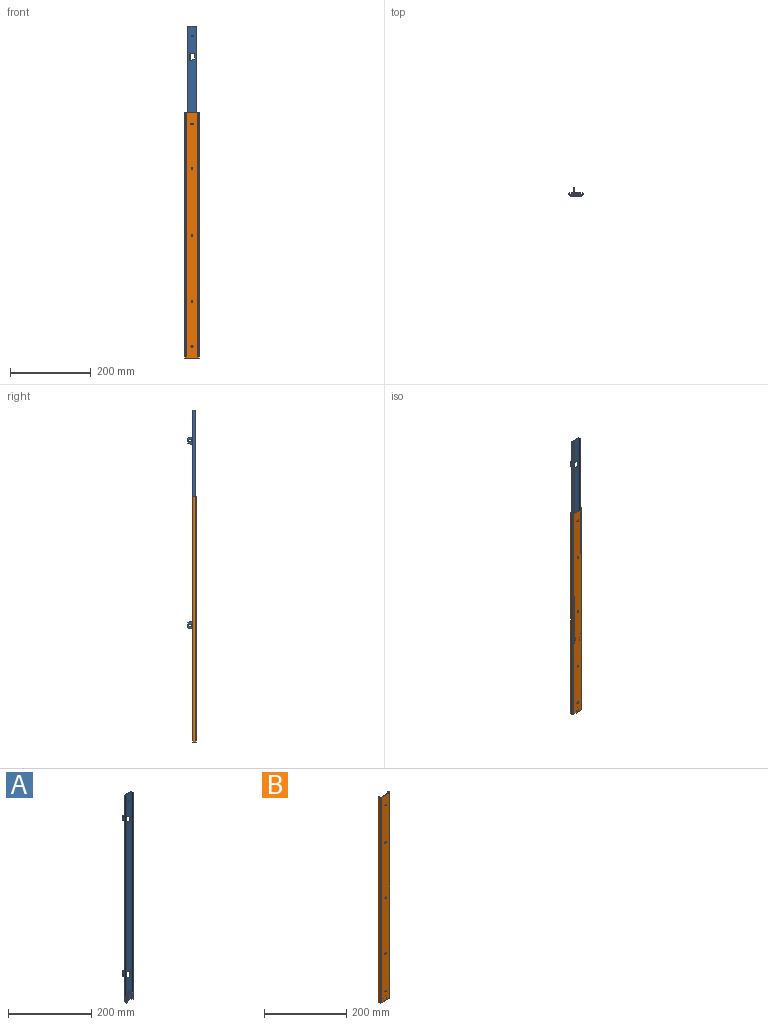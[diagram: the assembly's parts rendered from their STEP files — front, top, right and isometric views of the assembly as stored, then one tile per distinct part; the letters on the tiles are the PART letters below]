
ASSEMBLY  parts=2 mates=1
PART A: 102 faces, bbox 24.4x18.9x610 mm
  f0: plane 3.3x0.94mm, normal (0.82,0,0.57), area 3.8mm2, adj f8,f10,f28,f32
  f1: cylinder r=1mm len=3.3mm, axis (0,1,0), area 4.2mm2, adj f11,f12,f28,f32
  f2: cylinder r=1mm len=3.3mm, axis (0,1,0), area 3.2mm2, adj f7,f12,f28,f32
  f3: cylinder r=1mm len=3.3mm, axis (0,1,0), area 3.2mm2, adj f6,f13,f30,f32
  f4: cylinder r=1mm len=3.3mm, axis (0,1,0), area 4.2mm2, adj f13,f14,f30,f32
  f5: plane 3.3x0.94mm, normal (-0.82,0,0.57), area 3.8mm2, adj f9,f15,f30,f32
  f6: plane 3.3x0.17mm, normal (0.95,0,-0.3), area 0.6mm2, adj f3,f24,f30,f32
  f7: plane 3.3x0.17mm, normal (-0.95,0,-0.3), area 0.6mm2, adj f2,f26,f28,f32
  f8: cylinder r=1mm len=3.3mm, axis (0,1,0), area 4.2mm2, adj f0,f27,f28,f32
  f9: cylinder r=1mm len=3.3mm, axis (0,1,0), area 4.2mm2, adj f5,f29,f30,f32
  f10: cylinder r=1mm len=3.3mm, axis (0,1,0), area 10.4mm2, adj f0,f11,f28,f32
  f11: plane 3.3x2.58mm, normal (-0.82,0,-0.57), area 10.4mm2, adj f1,f10,f28,f32
  f12: plane 3.3x1.72mm, normal (-0.79,0,0.61), area 7.2mm2, adj f1,f2,f28,f32
  f13: plane 3.3x1.72mm, normal (0.79,0,0.61), area 7.2mm2, adj f3,f4,f30,f32
  f14: plane 3.3x2.58mm, normal (0.82,0,-0.57), area 10.4mm2, adj f4,f15,f30,f32
  f15: cylinder r=1mm len=3.3mm, axis (0,1,0), area 10.4mm2, adj f5,f14,f30,f32
  f16: cylinder r=1mm len=3.3mm, axis (0,1,0), area 4.2mm2, adj f19,f32,f34,f64
  f17: cylinder r=1mm len=3.3mm, axis (0,1,0), area 3.2mm2, adj f32,f33,f35,f64
  f18: cylinder r=1mm len=3.3mm, axis (0,1,0), area 4.2mm2, adj f32,f35,f36,f64
  f19: plane 3.3x0.94mm, normal (-0.82,0,-0.57), area 3.8mm2, adj f16,f32,f37,f64
  f20: cylinder r=1mm len=3.3mm, axis (0,1,0), area 4.2mm2, adj f21,f32,f38,f65
  f21: plane 3.3x0.94mm, normal (0.82,0,-0.57), area 3.8mm2, adj f20,f32,f39,f65
  f22: cylinder r=1mm len=3.3mm, axis (0,1,0), area 3.2mm2, adj f31,f32,f41,f65
  f23: cylinder r=1mm len=3.3mm, axis (0,1,0), area 4.2mm2, adj f32,f40,f41,f65
  f24: plane 4.8x2.5mm, normal (1,0,0), area 9.4mm2, adj f6,f25,f30,f32,f56
  f25: plane 13.8x1.5mm, normal (0,-0.71,0.71), area 29.3mm2, adj f24,f26,f32,f56
  f26: plane 4.8x2.5mm, normal (-1,0,0), area 9.4mm2, adj f7,f25,f28,f32,f56
  f27: plane 3.3x3.3mm, normal (0.79,0,-0.61), area 13.8mm2, adj f8,f28,f32,f58
  f28: plane 9.5x5.56mm, normal (0,-1,0), area 28.9mm2, adj f0,f1,f2,f7,f8,f10,f11,f12
  f29: plane 3.3x3.3mm, normal (-0.79,0,-0.61), area 13.8mm2, adj f9,f30,f32,f59
  f30: plane 9.5x5.56mm, normal (0,-1,0), area 28.9mm2, adj f3,f4,f5,f6,f9,f13,f14,f15
  f31: plane 3.3x0.17mm, normal (-0.95,0,0.3), area 0.6mm2, adj f22,f32,f61,f65
  f32: plane 21.6x16.5mm, normal (0,-1,0), area 268.1mm2, adj f0,f1,f2,f3,f4,f5,f6,f7
  f33: plane 3.3x0.17mm, normal (0.95,0,0.3), area 0.6mm2, adj f17,f32,f63,f64
  f34: plane 3.3x3.3mm, normal (-0.79,0,0.61), area 13.8mm2, adj f16,f32,f59,f64
  f35: plane 3.3x1.72mm, normal (0.79,0,-0.61), area 7.2mm2, adj f17,f18,f32,f64
  f36: plane 3.3x2.58mm, normal (0.82,0,0.57), area 10.4mm2, adj f18,f32,f37,f64
  f37: cylinder r=1mm len=3.3mm, axis (0,1,0), area 10.4mm2, adj f19,f32,f36,f64
  f38: plane 3.3x3.3mm, normal (0.79,0,0.61), area 13.8mm2, adj f20,f32,f58,f65
  f39: cylinder r=1mm len=3.3mm, axis (0,1,0), area 10.4mm2, adj f21,f32,f40,f65
  f40: plane 3.3x2.58mm, normal (-0.82,0,0.57), area 10.4mm2, adj f23,f32,f39,f65
  f41: plane 3.3x1.72mm, normal (-0.79,0,-0.61), area 7.2mm2, adj f22,f23,f32,f65
  f42: cylinder r=2mm len=1.99mm, axis (-1,0,0), area 4.1mm2, adj f44,f70,f71,f85
  f43: cylinder r=2mm len=1.99mm, axis (-1,0,0), area 4.1mm2, adj f44,f70,f71,f87
  f44: plane 11.68x1.4mm, normal (0,1,0), area 16.3mm2, adj f42,f43,f70,f71
  f45: cylinder r=2.45mm len=4.9mm, axis (-1,0,0), area 10.8mm2, adj f46,f48,f70,f71
  f46: plane 3x1.4mm, normal (0,0,1), area 4.2mm2, adj f45,f47,f70,f71
  f47: cylinder r=2.45mm len=4.9mm, axis (-1,0,0), area 10.8mm2, adj f46,f48,f70,f71
  f48: plane 3x1.4mm, normal (0,0,-1), area 4.2mm2, adj f45,f47,f70,f71
  f49: cylinder r=2mm len=1.99mm, axis (-1,0,0), area 4.1mm2, adj f51,f73,f74,f93
  f50: cylinder r=2mm len=1.99mm, axis (-1,0,0), area 4.1mm2, adj f51,f73,f74,f95
  f51: plane 11.68x1.4mm, normal (0,1,0), area 16.3mm2, adj f49,f50,f73,f74
  f52: cylinder r=2.45mm len=4.9mm, axis (-1,0,0), area 10.8mm2, adj f53,f55,f73,f74
  f53: plane 3x1.4mm, normal (0,0,-1), area 4.2mm2, adj f52,f54,f73,f74
  f54: cylinder r=2.45mm len=4.9mm, axis (-1,0,0), area 10.8mm2, adj f53,f55,f73,f74
  f55: plane 3x1.4mm, normal (0,0,1), area 4.2mm2, adj f52,f54,f73,f74
  f56: plane 21.6x5.2mm, normal (0,0,1), area 46.1mm2, adj f24,f25,f26,f28,f30,f58,f59,f75
  f57: plane 610x1.4mm, normal (0,-1,0), area 854mm2, adj f59,f77,f78,f80
  f58: plane 610x5.3mm, normal (-1,0,0), area 3178.5mm2, adj f27,f28,f32,f38,f56,f60,f65,f75
  f59: plane 610x5.3mm, normal (1,0,0), area 3178.5mm2, adj f29,f30,f32,f34,f56,f57,f64,f75
  f60: plane 610x1.4mm, normal (0,-1,0), area 854mm2, adj f58,f78,f79,f80
  f61: plane 5.3x2.5mm, normal (-1,0,0), area 10.2mm2, adj f31,f32,f62,f65,f80
  f62: plane 13.8x2mm, normal (0,-0.71,-0.71), area 39mm2, adj f32,f61,f63,f80
  f63: plane 5.3x2.5mm, normal (1,0,0), area 10.2mm2, adj f32,f33,f62,f64,f80
  f64: plane 9.5x5.56mm, normal (0,-1,0), area 28.9mm2, adj f16,f17,f18,f19,f33,f34,f35,f36
  f65: plane 9.5x5.56mm, normal (0,-1,0), area 28.9mm2, adj f20,f21,f22,f23,f31,f38,f39,f40
  f66: plane 1.4x0.7mm, normal (0,0,1), area 1mm2, adj f75,f81,f82,f101
  f67: plane 1.4x0.7mm, normal (0,0,-1), area 1mm2, adj f75,f81,f82,f101
  f68: plane 1.4x0.7mm, normal (0,0,1), area 1mm2, adj f75,f83,f84,f101
  f69: plane 1.4x0.7mm, normal (0,0,-1), area 1mm2, adj f75,f83,f84,f101
  f70: plane 17.68x10.8mm, normal (-1,0,0), area 143mm2, adj f42,f43,f44,f45,f46,f47,f48,f85
  f71: plane 18x12.2mm, normal (1,0,0), area 168mm2, adj f42,f43,f44,f45,f46,f47,f48,f72
  f72: cylinder r=1.4mm len=18.32mm, axis (0,0,-1), area 39.8mm2, adj f71,f75,f88,f92
  f73: plane 17.68x10.8mm, normal (-1,0,0), area 143mm2, adj f49,f50,f51,f52,f53,f54,f55,f93
  f74: plane 18x12.2mm, normal (1,0,0), area 168mm2, adj f49,f50,f51,f52,f53,f54,f55,f76
  f75: plane 590x21.6mm, normal (0,-1,0), area 12284.3mm2, adj f56,f58,f59,f66,f67,f68,f69,f72
  f76: cylinder r=1.4mm len=18.32mm, axis (0,0,-1), area 39.8mm2, adj f74,f75,f96,f100
  f77: plane 610x6.7mm, normal (-1,0,0), area 4087mm2, adj f57,f78,f80,f101
  f78: plane 24.4x6.7mm, normal (0,0,1), area 49mm2, adj f57,f58,f59,f60,f75,f77,f79,f101
  f79: plane 610x6.7mm, normal (1,0,0), area 4087mm2, adj f60,f78,f80,f101
  f80: plane 24.4x6.7mm, normal (0,0,-1), area 88.2mm2, adj f57,f58,f59,f60,f61,f62,f63,f64
  f81: cylinder r=2.3mm len=4.6mm, axis (0,1,0), area 10.1mm2, adj f66,f67,f75,f101
  f82: cylinder r=2.3mm len=4.6mm, axis (0,1,0), area 10.1mm2, adj f66,f67,f75,f101
  f83: cylinder r=2.3mm len=4.6mm, axis (0,1,0), area 10.1mm2, adj f68,f69,f75,f101
  f84: cylinder r=2.3mm len=4.6mm, axis (0,1,0), area 10.1mm2, adj f68,f69,f75,f101
  f85: plane 10.42x2.8mm, normal (0,0.11,0.99), area 15.1mm2, adj f42,f70,f71,f86,f101
  f86: cylinder r=1.4mm len=18mm, axis (0,0,1), area 39.3mm2, adj f70,f85,f87,f101
  f87: plane 10.42x2.8mm, normal (0,0.11,-0.99), area 15.1mm2, adj f43,f70,f71,f86,f101
  f88: plane 10.72x1.4mm, normal (-0.11,0,0.99), area 13.6mm2, adj f72,f75,f89,f101
  f89: cylinder r=2mm len=1.99mm, axis (0,1,0), area 4.1mm2, adj f75,f88,f90,f101
  f90: plane 11.93x1.4mm, normal (-1,0,0), area 16.7mm2, adj f75,f89,f91,f101
  f91: cylinder r=2mm len=1.99mm, axis (0,1,0), area 4.1mm2, adj f75,f90,f92,f101
  f92: plane 10.72x1.4mm, normal (-0.11,0,-0.99), area 13.6mm2, adj f72,f75,f91,f101
  f93: plane 10.42x2.8mm, normal (0,0.11,0.99), area 15.1mm2, adj f49,f73,f74,f94,f101
  f94: cylinder r=1.4mm len=18mm, axis (0,0,1), area 39.3mm2, adj f73,f93,f95,f101
  f95: plane 10.42x2.8mm, normal (0,0.11,-0.99), area 15.1mm2, adj f50,f73,f74,f94,f101
  f96: plane 10.72x1.4mm, normal (-0.11,0,0.99), area 13.6mm2, adj f75,f76,f97,f101
  f97: cylinder r=2mm len=1.99mm, axis (0,1,0), area 4.1mm2, adj f75,f96,f98,f101
  f98: plane 11.93x1.4mm, normal (-1,0,0), area 16.7mm2, adj f75,f97,f99,f101
  f99: cylinder r=2mm len=1.99mm, axis (0,1,0), area 4.1mm2, adj f75,f98,f100,f101
  f100: plane 10.72x1.4mm, normal (-0.11,0,-0.99), area 13.6mm2, adj f75,f76,f99,f101
  f101: plane 610x24.4mm, normal (0,1,0), area 14374.3mm2, adj f66,f67,f68,f69,f77,f78,f79,f80
PART B: 43 faces, bbox 35.1x8.5x610 mm
  f0: plane 13.6x11.4mm, normal (0,1,0), area 110.9mm2, adj f3,f4,f5,f6,f7,f8,f9,f10
  f1: plane 610x1.09mm, normal (0.63,0.77,0), area 856.5mm2, adj f13,f14,f18,f20
  f2: plane 610x1.09mm, normal (-0.63,0.77,0), area 856.5mm2, adj f12,f16,f18,f20
  f3: cylinder r=3mm len=5.21mm, axis (0,-1,0), area 31.3mm2, adj f0,f4,f10,f17
  f4: plane 4.6x2.61mm, normal (-1,0,0), area 12mm2, adj f0,f3,f5,f17
  f5: cylinder r=3.12mm len=6.25mm, axis (0,-1,0), area 45.2mm2, adj f0,f4,f6,f17
  f6: plane 4.6x2.61mm, normal (1,0,0), area 12mm2, adj f0,f5,f7,f17
  f7: cylinder r=3mm len=5.21mm, axis (0,-1,0), area 31.3mm2, adj f0,f6,f8,f17
  f8: plane 4.6x2.66mm, normal (1,0,0), area 12.3mm2, adj f0,f7,f9,f17
  f9: plane 9.4x4.6mm, normal (0,0,1), area 43.2mm2, adj f0,f8,f10,f17
  f10: plane 4.6x2.66mm, normal (-1,0,0), area 12.3mm2, adj f0,f3,f9,f17
  f11: plane 610x1.39mm, normal (-0.63,0.77,0), area 1097.7mm2, adj f12,f17,f18,f20
  f12: cylinder r=3.44mm len=610mm, axis (0,0,1), area 3483.5mm2, adj f2,f11,f18,f20
  f13: cylinder r=4.84mm len=610mm, axis (0,0,1), area 4824.8mm2, adj f1,f18,f19,f20
  f14: cylinder r=3.44mm len=610mm, axis (0,0,1), area 3483.5mm2, adj f1,f15,f18,f20
  f15: plane 610x1.39mm, normal (0.63,0.77,0), area 1097.7mm2, adj f14,f17,f18,f20
  f16: cylinder r=4.84mm len=610mm, axis (0,0,1), area 4824.8mm2, adj f2,f18,f20,f21
  f17: plane 610x27mm, normal (0,1,0), area 16259.3mm2, adj f3,f4,f5,f6,f7,f8,f9,f10
  f18: plane 35.1x8.5mm, normal (0,0,1), area 63.3mm2, adj f1,f2,f11,f12,f13,f14,f15,f16
  f19: plane 610x1.78mm, normal (-0.63,-0.77,0), area 1402.9mm2, adj f13,f18,f20,f42
  f20: plane 35.1x8.5mm, normal (0,0,-1), area 63.3mm2, adj f1,f2,f11,f12,f13,f14,f15,f16
  f21: plane 610x1.78mm, normal (0.63,-0.77,0), area 1402.9mm2, adj f16,f18,f20,f42
  f22: cylinder r=2.3mm len=4.6mm, axis (0,-1,0), area 10.1mm2, adj f17,f23,f25,f42
  f23: plane 1.4x0.7mm, normal (0,0,-1), area 1mm2, adj f17,f22,f24,f42
  f24: cylinder r=2.3mm len=4.6mm, axis (0,-1,0), area 10.1mm2, adj f17,f23,f25,f42
  f25: plane 1.4x0.7mm, normal (0,0,1), area 1mm2, adj f17,f22,f24,f42
  f26: cylinder r=2.3mm len=4.6mm, axis (0,-1,0), area 10.1mm2, adj f17,f27,f29,f42
  f27: plane 1.4x0.7mm, normal (0,0,-1), area 1mm2, adj f17,f26,f28,f42
  f28: cylinder r=2.3mm len=4.6mm, axis (0,-1,0), area 10.1mm2, adj f17,f27,f29,f42
  f29: plane 1.4x0.7mm, normal (0,0,1), area 1mm2, adj f17,f26,f28,f42
  f30: plane 1.4x0.7mm, normal (-1,0,0), area 1mm2, adj f17,f31,f33,f42
  f31: cylinder r=2.3mm len=4.6mm, axis (0,-1,0), area 10.1mm2, adj f17,f30,f32,f42
  f32: plane 1.4x0.7mm, normal (1,0,0), area 1mm2, adj f17,f31,f33,f42
  f33: cylinder r=2.3mm len=4.6mm, axis (0,-1,0), area 10.1mm2, adj f17,f30,f32,f42
  f34: plane 1.4x0.7mm, normal (1,0,0), area 1mm2, adj f17,f35,f37,f42
  f35: cylinder r=2.3mm len=4.6mm, axis (0,-1,0), area 10.1mm2, adj f17,f34,f36,f42
  f36: plane 1.4x0.7mm, normal (-1,0,0), area 1mm2, adj f17,f35,f37,f42
  f37: cylinder r=2.3mm len=4.6mm, axis (0,-1,0), area 10.1mm2, adj f17,f34,f36,f42
  f38: cylinder r=2.3mm len=4.6mm, axis (0,-1,0), area 10.1mm2, adj f17,f39,f41,f42
  f39: plane 1.4x0.7mm, normal (1,0,0), area 1mm2, adj f17,f38,f40,f42
  f40: cylinder r=2.3mm len=4.6mm, axis (0,-1,0), area 10.1mm2, adj f17,f39,f41,f42
  f41: plane 1.4x0.7mm, normal (-1,0,0), area 1mm2, adj f17,f38,f40,f42
  f42: plane 610x28mm, normal (0,-1,0), area 16980.8mm2, adj f18,f19,f20,f21,f22,f23,f24,f25
PLACE A t=(43.53,-9.42,725.43)mm fixed
PLACE B t=(-8.88,-8.02,86.73)mm
MATE planar B.f17 <-> A.f60  axis (0,1,0) through (-0.49,-13.81,-383.57)mm
